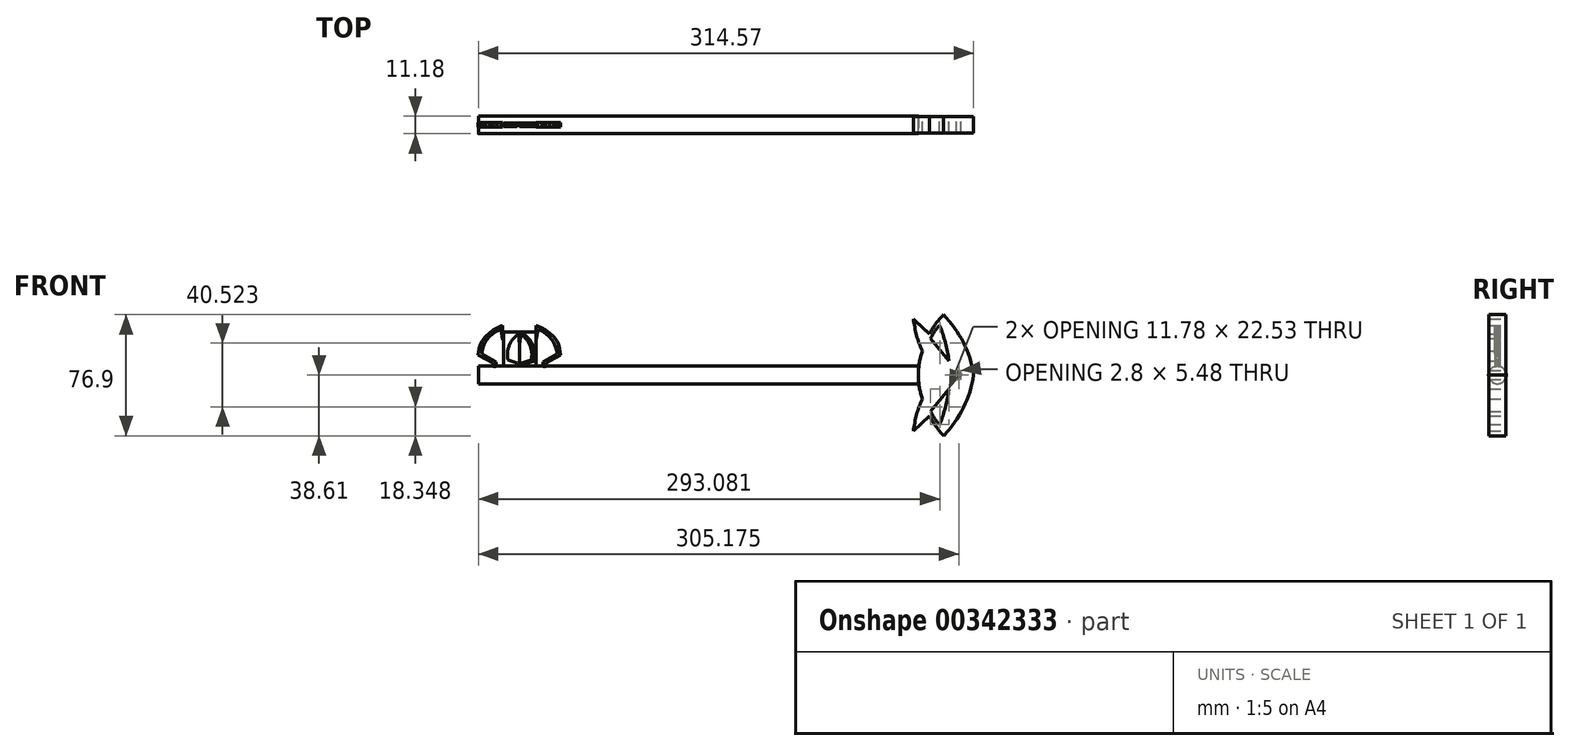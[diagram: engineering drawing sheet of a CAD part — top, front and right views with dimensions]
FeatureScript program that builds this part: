
annotation { "Feature Type Name" : "Feature", "Feature Type Description" : "" }
export const myFeature = defineFeature(function(context is Context, id is Id, definition is map)
    precondition{}
    {
        {
            var Q0;
            Q0=qCreatedBy(makeId("Right.planeOp"),FACE);
            var sketch = newSketch(context, id + "F0", { "sketchPlane" : qUnion([Q0])});
            skCircle(sketch, "E0", {"center": v(0, 0) * mm, "radius": 5.6 * mm});
            skSolve(sketch);
        }
        {
            var Q0;
            Q0 = qSketchRegion(id + "F0", true);
            extrude(context, id + "F1", {"entities" : qUnion([Q0]), "oppositeDirection" : true, "depth" : 279.4 * mm});
        }
        {
            var Q0;
            Q0=qCreatedBy(makeId("Front.planeOp"),FACE);
            var sketch = newSketch(context, id + "F2", { "sketchPlane" : qUnion([Q0])});
            skLineSegment(sketch, "E1", {"start": v(-279.4, 12.86) * mm, "end": v(-270.02, 7.64) * mm});
            skLineSegment(sketch, "E2", {"start": v(-270.02, 7.64) * mm, "end": v(-270.02, 5.61) * mm});
            skLineSegment(sketch, "E3", {"start": v(-277.1, 21.72) * mm, "end": v(-278.1, 19.58) * mm});
            skLineSegment(sketch, "E4", {"start": v(-278.1, 19.58) * mm, "end": v(-278.83, 16.92) * mm});
            skLineSegment(sketch, "E5", {"start": v(-278.83, 16.92) * mm, "end": v(-279.4, 12.86) * mm});
            skLineSegment(sketch, "E6", {"start": v(-277, 13.43) * mm, "end": v(-277, 14.84) * mm});
            skLineSegment(sketch, "E7", {"start": v(-277, 14.84) * mm, "end": v(-276.33, 17.76) * mm});
            skLineSegment(sketch, "E8", {"start": v(-276.33, 17.76) * mm, "end": v(-274.97, 20.94) * mm});
            skLineSegment(sketch, "E9", {"start": v(-274.97, 20.94) * mm, "end": v(-272.47, 24.01) * mm});
            skLineSegment(sketch, "E10", {"start": v(-272.47, 24.01) * mm, "end": v(-270.23, 25.94) * mm});
            skLineSegment(sketch, "E11", {"start": v(-270.23, 25.94) * mm, "end": v(-267.62, 27.87) * mm});
            skLineSegment(sketch, "E12", {"start": v(-277, 13.43) * mm, "end": v(-268.1, 8.17) * mm});
            skLineSegment(sketch, "E13", {"start": v(-268.1, 8.17) * mm, "end": v(-268.1, 5.66) * mm});
            skLineSegment(sketch, "E14", {"start": v(-277.1, 21.72) * mm, "end": v(-274.82, 24.53) * mm});
            skLineSegment(sketch, "E15", {"start": v(-274.82, 24.53) * mm, "end": v(-272.37, 26.72) * mm});
            skLineSegment(sketch, "E16", {"start": v(-272.37, 26.72) * mm, "end": v(-269.92, 28.5) * mm});
            skLineSegment(sketch, "E17", {"start": v(-269.92, 28.5) * mm, "end": v(-267.62, 29.85) * mm});
            skLineSegment(sketch, "E18", {"start": v(-267.62, 29.85) * mm, "end": v(-264.86, 31.05) * mm});
            skLineSegment(sketch, "E19", {"start": v(-264.86, 31.05) * mm, "end": v(-263.87, 31.46) * mm});
            skLineSegment(sketch, "E20", {"start": v(-263.87, 31.46) * mm, "end": v(-263.87, 22.13) * mm});
            skLineSegment(sketch, "E21", {"start": v(-267.62, 27.87) * mm, "end": v(-264.91, 28.96) * mm});
            skLineSegment(sketch, "E22", {"start": v(-264.91, 28.96) * mm, "end": v(-263.87, 22.13) * mm});
            skLineSegment(sketch, "E23.MirrorCS", {"start": v(-236.6, 28.5) * mm, "end": v(-238.89, 29.85) * mm});
            skLineSegment(sketch, "E24.MirrorCS", {"start": v(-229.4, 21.72) * mm, "end": v(-228.41, 19.58) * mm});
            skLineSegment(sketch, "E25.MirrorCS", {"start": v(-234.04, 24.01) * mm, "end": v(-236.28, 25.94) * mm});
            skLineSegment(sketch, "E26.MirrorCS", {"start": v(-229.5, 13.43) * mm, "end": v(-229.5, 14.84) * mm});
            skLineSegment(sketch, "E27.MirrorCS", {"start": v(-234.15, 26.72) * mm, "end": v(-236.6, 28.5) * mm});
            skLineSegment(sketch, "E28.MirrorCS", {"start": v(-241.65, 31.05) * mm, "end": v(-242.64, 31.46) * mm});
            skLineSegment(sketch, "E29.MirrorCS", {"start": v(-238.42, 8.17) * mm, "end": v(-238.42, 5.66) * mm});
            skLineSegment(sketch, "E30.MirrorCS", {"start": v(-236.28, 25.94) * mm, "end": v(-238.89, 27.87) * mm});
            skLineSegment(sketch, "E31.MirrorCS", {"start": v(-238.89, 27.87) * mm, "end": v(-241.6, 28.96) * mm});
            skLineSegment(sketch, "E32.MirrorCS", {"start": v(-242.64, 31.46) * mm, "end": v(-242.64, 22.13) * mm});
            skLineSegment(sketch, "E33.MirrorCS", {"start": v(-231.7, 24.53) * mm, "end": v(-234.15, 26.72) * mm});
            skLineSegment(sketch, "E34.MirrorCS", {"start": v(-229.5, 13.43) * mm, "end": v(-238.42, 8.17) * mm});
            skLineSegment(sketch, "E35.MirrorCS", {"start": v(-231.54, 20.94) * mm, "end": v(-234.04, 24.01) * mm});
            skLineSegment(sketch, "E36.MirrorCS", {"start": v(-228.41, 19.58) * mm, "end": v(-227.68, 16.92) * mm});
            skLineSegment(sketch, "E37.MirrorCS", {"start": v(-241.6, 28.96) * mm, "end": v(-242.64, 22.13) * mm});
            skLineSegment(sketch, "E38.MirrorCS", {"start": v(-236.5, 7.64) * mm, "end": v(-236.5, 5.61) * mm});
            skLineSegment(sketch, "E39.MirrorCS", {"start": v(-230.18, 17.76) * mm, "end": v(-231.54, 20.94) * mm});
            skLineSegment(sketch, "E40.MirrorCS", {"start": v(-229.4, 21.72) * mm, "end": v(-231.7, 24.53) * mm});
            skLineSegment(sketch, "E41.MirrorCS", {"start": v(-229.5, 14.84) * mm, "end": v(-230.18, 17.76) * mm});
            skLineSegment(sketch, "E42.MirrorCS", {"start": v(-238.89, 29.85) * mm, "end": v(-241.65, 31.05) * mm});
            skLineSegment(sketch, "E43.MirrorCS", {"start": v(-227.68, 16.92) * mm, "end": v(-227.1, 12.86) * mm});
            skLineSegment(sketch, "E44.MirrorCS", {"start": v(-227.1, 12.86) * mm, "end": v(-236.5, 7.64) * mm});
            skLineSegment(sketch, "E45", {"start": v(-270.02, 5.61) * mm, "end": v(-270.02, 0) * mm});
            skLineSegment(sketch, "E46", {"start": v(-270.02, 0) * mm, "end": v(-236.4, 0) * mm});
            skLineSegment(sketch, "E47", {"start": v(-236.4, 0) * mm, "end": v(-236.5, 5.61) * mm});
            skLineSegment(sketch, "E48", {"start": v(-238.42, 5.66) * mm, "end": v(-238.42, 1.69) * mm});
            skLineSegment(sketch, "E49", {"start": v(-238.42, 1.69) * mm, "end": v(-268.23, 1.69) * mm});
            skLineSegment(sketch, "E50", {"start": v(-268.23, 1.69) * mm, "end": v(-268.1, 5.66) * mm});
            skSolve(sketch);
        }
        {
            var Q0;
            Q0=qCreatedBy(makeId("Front.planeOp"),FACE);
            var sketch = newSketch(context, id + "F3", { "sketchPlane" : qUnion([Q0])});
            skPoint(sketch, "E51.start.orphan", {"position": v(0, 0) * mm});
            skLineSegment(sketch, "E52", {"start": v(-0.2, 0) * mm, "end": v(0, 0) * mm});
            skPoint(sketch, "E53.start.orphan", {"position": v(-0.1, 0) * mm});
            skArc(sketch, "E54", {"start": v(0.01, -0.29) * mm, "mid": v(-0.1, -0.14) * mm, "end": v(-0.2, 0) * mm});
            skArc(sketch, "E55", {"start": v(15.91, 38.3) * mm, "mid": v(4.47, 20.6) * mm, "end": v(0, 0) * mm});
            skArc(sketch, "E56", {"start": v(0, 0) * mm, "mid": v(4.55, -20.8) * mm, "end": v(16.22, -38.61) * mm});
            skArc(sketch, "E57", {"start": v(-0.2, 0) * mm, "mid": v(-0.1, 0.14) * mm, "end": v(0.01, 0.28) * mm});
            skArc(sketch, "E58", {"start": v(-3.07, 35.56) * mm, "mid": v(-1, 25.2) * mm, "end": v(2.54, 15.24) * mm});
            skArc(sketch, "E59", {"start": v(-3.07, 35.56) * mm, "mid": v(1.92, 30.73) * mm, "end": v(7.09, 26.09) * mm});
            skLineSegment(sketch, "E60", {"start": v(15.91, 38.3) * mm, "end": v(23.93, 5.93) * mm});
            skLineSegment(sketch, "E61", {"start": v(-3.07, -35.56) * mm, "end": v(7.1, -26.1) * mm});
            skArc(sketch, "E62", {"start": v(2.54, -15.24) * mm, "mid": v(-1, -25.2) * mm, "end": v(-3.07, -35.56) * mm});
            skLineSegment(sketch, "E63", {"start": v(23.93, 5.93) * mm, "end": v(19.85, 0) * mm});
            skLineSegment(sketch, "E64", {"start": v(23.65, -6.11) * mm, "end": v(16.22, -38.61) * mm});
            skLineSegment(sketch, "E65", {"start": v(19.85, 0) * mm, "end": v(23.65, -6.11) * mm});
            skPoint(sketch, "E66.end.orphan", {"position": v(27.17, 0) * mm});
            skLineSegment(sketch, "E67", {"start": v(27.17, 0) * mm, "end": v(24.38, 2.74) * mm});
            skLineSegment(sketch, "E68", {"start": v(24.38, 2.74) * mm, "end": v(24.38, -2.74) * mm});
            skLineSegment(sketch, "E69", {"start": v(24.38, -2.74) * mm, "end": v(27.17, 0) * mm});
            skLineSegment(sketch, "E70", {"start": v(2.54, 15.24) * mm, "end": v(2.54, -15.24) * mm});
            skArc(sketch, "E71", {"start": v(13.59, -31.53) * mm, "mid": v(17.27, -20.44) * mm, "end": v(19.57, -9) * mm});
            skArc(sketch, "E72", {"start": v(7.79, -23.06) * mm, "mid": v(10.3, -27.55) * mm, "end": v(13.59, -31.53) * mm});
            skLineSegment(sketch, "E73", {"start": v(7.79, -23.06) * mm, "end": v(19.57, -9) * mm});
            skLineSegment(sketch, "E74.MirrorCS", {"start": v(7.79, 23.06) * mm, "end": v(19.57, 9) * mm});
            skArc(sketch, "E75.MirrorCS", {"start": v(13.59, 31.53) * mm, "mid": v(17.27, 20.44) * mm, "end": v(19.57, 9) * mm});
            skArc(sketch, "E76.MirrorCS", {"start": v(7.79, 23.06) * mm, "mid": v(10.3, 27.55) * mm, "end": v(13.59, 31.53) * mm});
            skArc(sketch, "E77", {"start": v(16.22, -38.61) * mm, "mid": v(28.68, -20.77) * mm, "end": v(35.17, 0) * mm});
            skArc(sketch, "E78", {"start": v(35.17, 0) * mm, "mid": v(28.65, 20.7) * mm, "end": v(15.91, 38.3) * mm});
            skSolve(sketch);
        }
        {
            var Q0;
            Q0=qCreatedBy(makeId("Front.planeOp"),FACE);
            var sketch = newSketch(context, id + "F4", { "sketchPlane" : qUnion([Q0])});
            skLineSegment(sketch, "E79.top", {"start": v(-263.46, 5.6) * mm, "end": v(-243.55, 5.6) * mm});
            skLineSegment(sketch, "E79.left", {"start": v(-263.46, 22.24) * mm, "end": v(-263.46, 5.6) * mm});
            skLineSegment(sketch, "E80.bottom", {"start": v(-263.46, 5.6) * mm, "end": v(-242.88, 5.6) * mm});
            skLineSegment(sketch, "E80.top", {"start": v(-263.46, 27.29) * mm, "end": v(-242.88, 27.29) * mm});
            skLineSegment(sketch, "E80.left", {"start": v(-263.46, 5.6) * mm, "end": v(-263.46, 27.29) * mm});
            skLineSegment(sketch, "E80.right", {"start": v(-242.88, 5.6) * mm, "end": v(-242.88, 27.29) * mm});
            skSolve(sketch);
        }
        {
            var Q0;
            Q0 = qSketchRegion(id + "F2", true);
            extrude(context, id + "F5", {"entities" : qUnion([Q0]), "operationType" : NewBodyOperationType.ADD, "endBound" : BoundingType.SYMMETRIC, "depth" : 3 * mm});
        }
        {
            var Q0;
            Q0 = qSketchRegion(id + "F3", true);
            extrude(context, id + "F6", {"entities" : qUnion([Q0]), "operationType" : NewBodyOperationType.ADD, "endBound" : BoundingType.SYMMETRIC, "depth" : 10.67 * mm});
        }
        {
            var Q0;
            {var subQ4=sQuery(id+"F4.wireOp",EDGE,"E80.top");Q0=makeQuery(id+"F4.imprint","IMPRINT",FACE,{"disambiguationData":[TD([[makeQuery(id+"F4.imprint","IMPRINT",EDGE,{"derivedFrom":subQ4}),-1.0]])]});}
            extrude(context, id + "F7", {"entities" : qUnion([Q0]), "endBound" : BoundingType.SYMMETRIC, "depth" : 3.56 * mm, "offsetDistance" : 25.4 * mm});
        }
        {
            var Q0;
            Q0=makeQuery(id+"F7.opExtrude","CAP_EDGE",EDGE,{"disambiguationData":[OSD([sQuery(id+"F4.wireOp",EDGE,"E80.top")])],"isStart":false});
            var Q1;
            Q1=makeQuery(id+"F7.opExtrude","CAP_EDGE",EDGE,{"disambiguationData":[OSD([sQuery(id+"F4.wireOp",EDGE,"E80.top")])],"isStart":true});
            chamfer(context, id + "F8", {"entities" : qUnion([Q0, Q1]), "chamferType" : ChamferType.TWO_OFFSETS, "width1" : 1.78 * mm, "oppositeDirection" : false, "width2" : 33.02 * mm, "tangentPropagation" : true});
        }
        {
            var Q0;
            {var subQ0=sQuery(id+"F4.wireOp",EDGE,"E80.top");Q0=makeQuery(id+"F8.opChamfer","BLEND_FACE",FACE,{"disambiguationData":[OSD([subQ0]),TDD([makeQuery(id+"F7.opExtrude","CAP_EDGE",EDGE,{"disambiguationData":[OSD([subQ0])],"isStart":false})])]});}
            var sketch = newSketch(context, id + "F9", { "sketchPlane" : qUnion([Q0])});
            skLineSegment(sketch, "E81", {"start": v(-251.62, 5.53) * mm, "end": v(-251.62, 7.45) * mm});
            skLineSegment(sketch, "E82", {"start": v(-251.62, 7.45) * mm, "end": v(-245.78, 9.52) * mm});
            skLineSegment(sketch, "E83", {"start": v(-250.3, 7.05) * mm, "end": v(-250.3, 5.53) * mm});
            skArc(sketch, "E84", {"start": v(-245.78, 9.52) * mm, "mid": v(-246.55, 18.73) * mm, "end": v(-252.39, 25.9) * mm});
            skLineSegment(sketch, "E85", {"start": v(-250.3, 7.05) * mm, "end": v(-244.54, 8.47) * mm});
            skLineSegment(sketch, "E86", {"start": v(-253.17, 27.25) * mm, "end": v(-253.17, 19.2) * mm});
            skLineSegment(sketch, "E87", {"start": v(-253.17, 19.2) * mm, "end": v(-252.39, 25.9) * mm});
            skArc(sketch, "E88", {"start": v(-244.54, 8.47) * mm, "mid": v(-245.12, 19.58) * mm, "end": v(-253.17, 27.25) * mm});
            skLineSegment(sketch, "E89", {"start": v(-253.17, 27.25) * mm, "end": v(-253.17, 5.53) * mm});
            skArc(sketch, "E90.MirrorCS", {"start": v(-260.57, 9.52) * mm, "mid": v(-259.8, 18.73) * mm, "end": v(-253.96, 25.9) * mm});
            skLineSegment(sketch, "E91.MirrorCS", {"start": v(-253.17, 19.2) * mm, "end": v(-253.96, 25.9) * mm});
            skArc(sketch, "E92.MirrorCS", {"start": v(-261.8, 8.47) * mm, "mid": v(-261.22, 19.58) * mm, "end": v(-253.17, 27.25) * mm});
            skLineSegment(sketch, "E93.MirrorCS", {"start": v(-256.03, 7.05) * mm, "end": v(-261.8, 8.47) * mm});
            skLineSegment(sketch, "E94.MirrorCS", {"start": v(-254.72, 7.45) * mm, "end": v(-260.57, 9.52) * mm});
            skLineSegment(sketch, "E95.MirrorCS", {"start": v(-254.72, 5.53) * mm, "end": v(-254.72, 7.45) * mm});
            skLineSegment(sketch, "E96.MirrorCS", {"start": v(-256.03, 7.05) * mm, "end": v(-256.03, 5.53) * mm});
            skSolve(sketch);
        }
        {
            var Q0;
            Q0 = qSketchRegion(id + "F9", true);
            var Q1;
            Q1=makeQuery(id+"F9.imprint","IMPRINT",FACE,{"disambiguationData":[TD([[makeQuery(id+"F9.imprint","IMPRINT",EDGE,{"derivedFrom":sQuery(id+"F9.wireOp",EDGE,"E90.MirrorCS")}),1.0]])]});
            var Q2;
            {var subQ1=sQuery(id+"F9.wireOp",EDGE,"E81");Q2=makeQuery(id+"F9.imprint","IMPRINT",FACE,{"disambiguationData":[TD([[makeQuery(id+"F9.imprint","IMPRINT",EDGE,{"derivedFrom":subQ1}),-1.0]])]});}
            extrude(context, id + "F10", {"entities" : qUnion([Q0, Q1, Q2]), "operationType" : NewBodyOperationType.REMOVE, "endBound" : BoundingType.SYMMETRIC, "oppositeDirection" : true, "depth" : 25.4 * mm, "offsetDistance" : 25.4 * mm});
        }
    });
